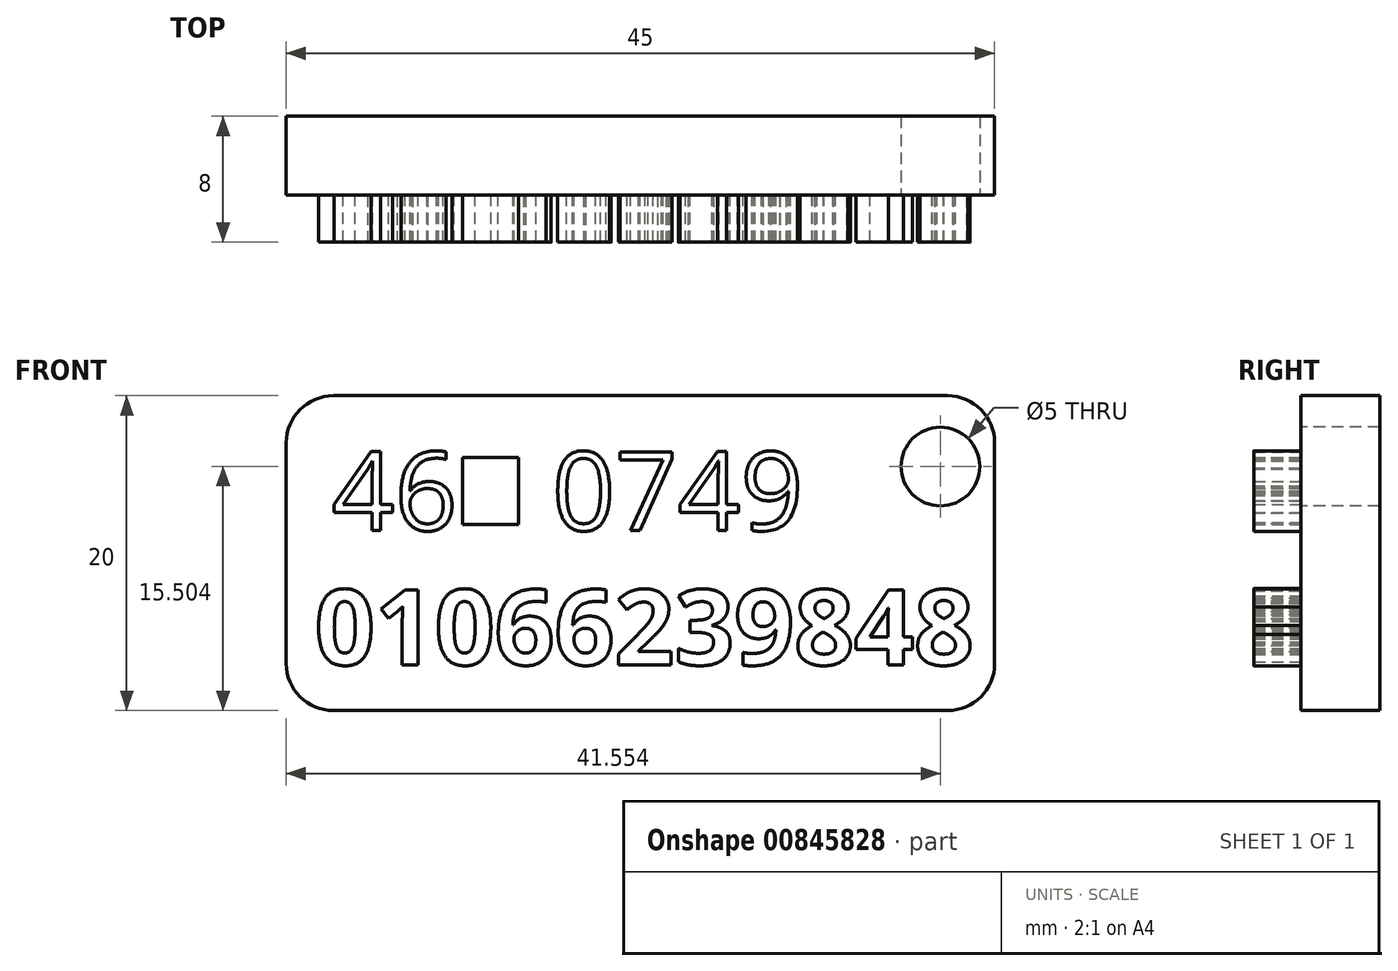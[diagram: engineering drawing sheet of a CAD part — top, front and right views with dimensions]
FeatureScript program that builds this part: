
annotation { "Feature Type Name" : "Feature", "Feature Type Description" : "" }
export const myFeature = defineFeature(function(context is Context, id is Id, definition is map)
    precondition{}
    {
        {
            var Q0;
            Q0=qCreatedBy(makeId("Front.planeOp"),FACE);
            var sketch = newSketch(context, id + "F0", { "sketchPlane" : qUnion([Q0])});
            skLineSegment(sketch, "E0.bottom", {"start": v(0, 20) * mm, "end": v(45, 20) * mm});
            skLineSegment(sketch, "E0.top", {"start": v(0, 0) * mm, "end": v(45, 0) * mm});
            skLineSegment(sketch, "E0.left", {"start": v(0, 20) * mm, "end": v(0, 0) * mm});
            skLineSegment(sketch, "E0.right", {"start": v(45, 20) * mm, "end": v(45, 0) * mm});
            skSolve(sketch);
        }
        {
            var Q0;
            Q0=makeQuery(id+"F0.imprint","IMPRINT",FACE,{"disambiguationData":[TD([[makeQuery(id+"F0.imprint","IMPRINT",EDGE,{"derivedFrom":sQuery(id+"F0.wireOp",EDGE,"E0.bottom")}),-1.0]])]});
            extrude(context, id + "F1", {"entities" : qUnion([Q0]), "depth" : 5 * mm, "offsetDistance" : 25 * mm});
        }
        {
            var Q0;
            Q0=makeQuery(id+"F1.opExtrude","CAP_FACE",FACE,{"disambiguationData":[OSD([sQuery(id+"F0.wireOp",EDGE,"E0.bottom"),sQuery(id+"F0.wireOp",EDGE,"E0.top"),sQuery(id+"F0.wireOp",EDGE,"E0.left"),sQuery(id+"F0.wireOp",EDGE,"E0.right")])],"isStart":false});
            var sketch = newSketch(context, id + "F2", { "sketchPlane" : qUnion([Q0])});
            skText(sketch, "E1", { "text": "46버 0749", "fontName": "OpenSans-Regular.ttf"});
            skText(sketch, "E2", { "text": "01066239848", "fontName": "OpenSans-Bold.ttf"});
            const initialGuessF2  = {"E1": [0.0029, 0.01145, 1, 0, 0.00502], "E2": [0.00182, 0.00291, 1, 0, 0.0048]};
            skSetInitialGuess(sketch, initialGuessF2);
            skSolve(sketch);
        }
        {
            var Q0;
            Q0 = qSketchRegion(id + "F2", true);
            extrude(context, id + "F3", {"entities" : qUnion([Q0]), "operationType" : NewBodyOperationType.ADD, "depth" : 3 * mm, "offsetDistance" : 25 * mm});
        }
        {
            var Q0;
            {var subQ0=sQuery(id+"F0.wireOp",EDGE,"E0.left");var subQ1=sQuery(id+"F0.wireOp",EDGE,"E0.bottom");var subQ2=sQuery(id+"F0.wireOp",EDGE,"E0.right");var subQ3=sQuery(id+"F0.wireOp",EDGE,"E0.top");Q0=makeQuery(id+"F3.boolean.opBoolean","SPLIT",FACE,{"disambiguationData":[TD([makeQuery(id+"F1.opExtrude","SWEPT_FACE",FACE,{"disambiguationData":[OSD([subQ1])]})])],"derivedFrom":makeQuery(id+"F1.opExtrude","CAP_FACE",FACE,{"disambiguationData":[OSD([subQ1,subQ3,subQ0,subQ2])],"isStart":false})});}
            var sketch = newSketch(context, id + "F4", { "sketchPlane" : qUnion([Q0])});
            skCircle(sketch, "E3", {"center": v(41.55, 15.5) * mm, "radius": 2.5 * mm});
            skSolve(sketch);
        }
        {
            var Q0;
            Q0 = qSketchRegion(id + "F4", true);
            extrude(context, id + "F5", {"entities" : qUnion([Q0]), "operationType" : NewBodyOperationType.REMOVE, "oppositeDirection" : true, "depth" : 25 * mm, "offsetDistance" : 25 * mm});
        }
        {
            var Q0;
            Q0=makeQuery(id+"F1.opExtrude","SWEPT_EDGE",EDGE,{"disambiguationData":[OSD([sQuery(id+"F0.wireOp",EDGE,"E0.bottom"),sQuery(id+"F0.wireOp",EDGE,"E0.left")])]});
            var Q1;
            Q1=makeQuery(id+"F1.opExtrude","SWEPT_EDGE",EDGE,{"disambiguationData":[OSD([sQuery(id+"F0.wireOp",EDGE,"E0.bottom"),sQuery(id+"F0.wireOp",EDGE,"E0.right")])]});
            var Q2;
            Q2=makeQuery(id+"F1.opExtrude","SWEPT_EDGE",EDGE,{"disambiguationData":[OSD([sQuery(id+"F0.wireOp",EDGE,"E0.top"),sQuery(id+"F0.wireOp",EDGE,"E0.right")])]});
            var Q3;
            Q3=makeQuery(id+"F1.opExtrude","SWEPT_EDGE",EDGE,{"disambiguationData":[OSD([sQuery(id+"F0.wireOp",EDGE,"E0.top"),sQuery(id+"F0.wireOp",EDGE,"E0.left")])]});
            fillet(context, id + "F6", {"entities" : qUnion([Q0, Q1, Q2, Q3]), "radius" : 3 * mm, "tangentPropagation" : true, "allowEdgeOverflow" : false});
        }
    });
